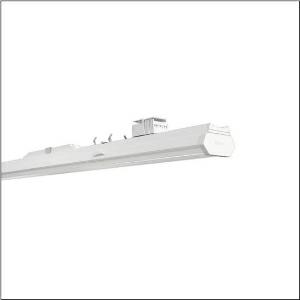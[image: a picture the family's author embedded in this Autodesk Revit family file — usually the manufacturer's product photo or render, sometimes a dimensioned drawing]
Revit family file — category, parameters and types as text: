
# Revit family: licross_r__11_protected_mo_51td12cn49xg_1fdf
name_source: partatom
category: Lighting Fixtures
units: mm (PartAtom-declared; Revit-internal decimal feet)

## family parameters
Cut with Voids When Loaded = No
Host = Face
Light Source = No
Part Type = Normal
Room Calculation Point = No
Round Connector Dimension = Use Diameter
Shared = No

## types (1)
- --- (1 x LED, 9070 lm, 49.4 W, 4000K)
    Apparent Load = 49 VA
    CIE Flux Codes = 73 92 98 99 100
    Color Rendering = 80
    Color Temperature = 4000K
    Default Elevation = 1800 mm
    Description = Licross® 11 Protected MO, luminaire insert, of sheet steel, galvanised, coil coated, white, length: 1.500mm, width: 90mm, height: 101mm, LED rated luminous flux: 9.070lm, light colour: 840, control gear: ON/OFF Multilumen, CLOi, with plug, 3-pole, with phase selection, mains connection: 220..240V, AC, 50/60Hz, halogen-free wiring, primary light control with lens, of plastic, primary optical cover: cover, of PMMA, light emission: direct with ceiling illumination distribution, primary light characteristic: symmetric, protection rating (complete): IP54, insulation class (complete): insulation class I (protective earthing), certification: CE, ENEC, VDE, UKCA, protection symbol: D if used in an environment with non-conductive dust loads with corresponding accessories, impact resistance: IK06, permissible ambient temperature for indoor applications: -35..+40°C, corresponds to IFS (International Featured Standards) requirements for safety and quality in the food industry, reducing of maximum allowable ambient temperature of 5°C with ceiling mounting, LABS conformity tested according to VDMA 24364:2018-05, packaging unit: 1 piece
    Height = 92 mm
    Lamp = 1 x LED
    Lamp Light Flux = 9070 lm
    Lamp Power = 49.4 W
    Lamp count = 1
    Length = 1500 mm
    Luminous efficacy = 184 lm/W
    Manufacturer = Siteco
    ModVariant = No
    Model = 51TD12CN49XG
    Mounting Place = Ceiling
    Mounting Type = Pendant
    Number of Poles = 1
    OnlyDefault = Yes
    Power Factor = 1
    Product Name = Licross® 11 Protected MO
    Product group = luminaire insert
    ProductGroupID = 902
    Protection Class = Protection class I
    Protection Degree = IP 54
    RLX_Detail_Level = 1
    RlxData = <blob elided: 22009 chars, md5=715bb0b1>
    Socket = socket
    Standby Power = 0 W
    System Light Flux = 9070 lm
    System Power = 49 W
    Type Comments = factory setting: luminous flux: 100 % | (A | C | E) | 113 mA
    Type Image = l_1256145.jpg
    URL = http://relux.com
    VarID = @adj_003835
    Voltage = 0 V
    Weight = 0.00 kg
    Width = 88 mm

## geometry (parser evidence)
native form markers: Blend x4, Sweep x10
no freeform markers — native parametric forms only
